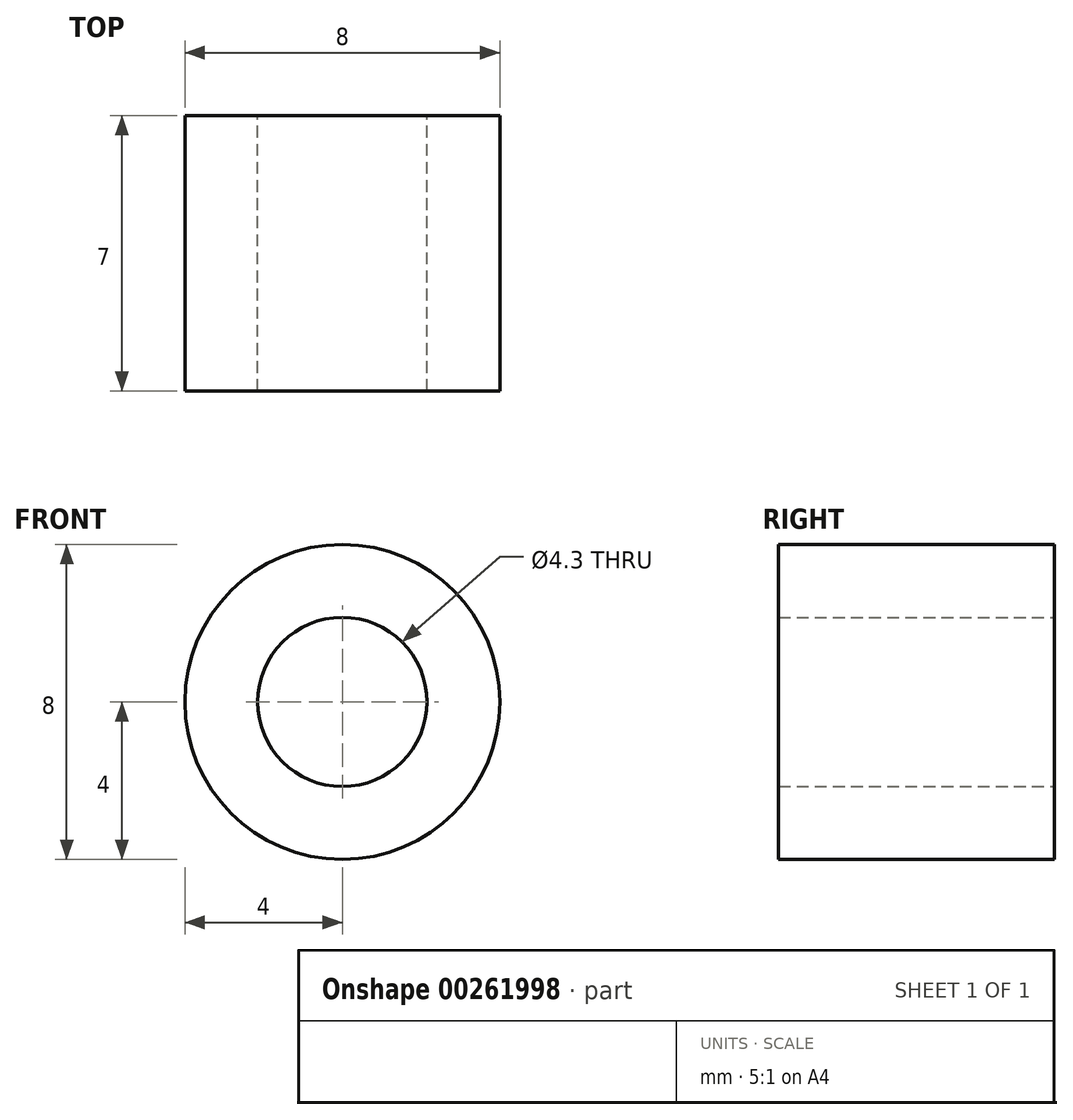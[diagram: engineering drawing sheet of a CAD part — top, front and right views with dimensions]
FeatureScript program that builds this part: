
annotation { "Feature Type Name" : "Feature", "Feature Type Description" : "" }
export const myFeature = defineFeature(function(context is Context, id is Id, definition is map)
    precondition{}
    {
        {
            assignVariable(context, id + "F0", {"name" : "Hieght", "anyValue" : 7});
        }
        {
            var Q0;
            Q0=qCreatedBy(makeId("Front.planeOp"),FACE);
            var sketch = newSketch(context, id + "F1", { "sketchPlane" : qUnion([Q0])});
            skCircle(sketch, "E0", {"center": v(0, 0) * mm, "radius": 2.15 * mm});
            skCircle(sketch, "E1", {"center": v(0, 0) * mm, "radius": 4 * mm});
            skSolve(sketch);
        }
        {
            var Q0;
            Q0=makeQuery(id+"F1.imprint","IMPRINT",FACE,{"disambiguationData":[TD([[makeQuery(id+"F1.imprint","IMPRINT",EDGE,{"derivedFrom":sQuery(id+"F1.wireOp",EDGE,"E0")}),-1.0]])]});
            extrude(context, id + "F2", {"entities" : qUnion([Q0]), "depth" : getVariable(context, 'Hieght') * mm});
        }
    });
